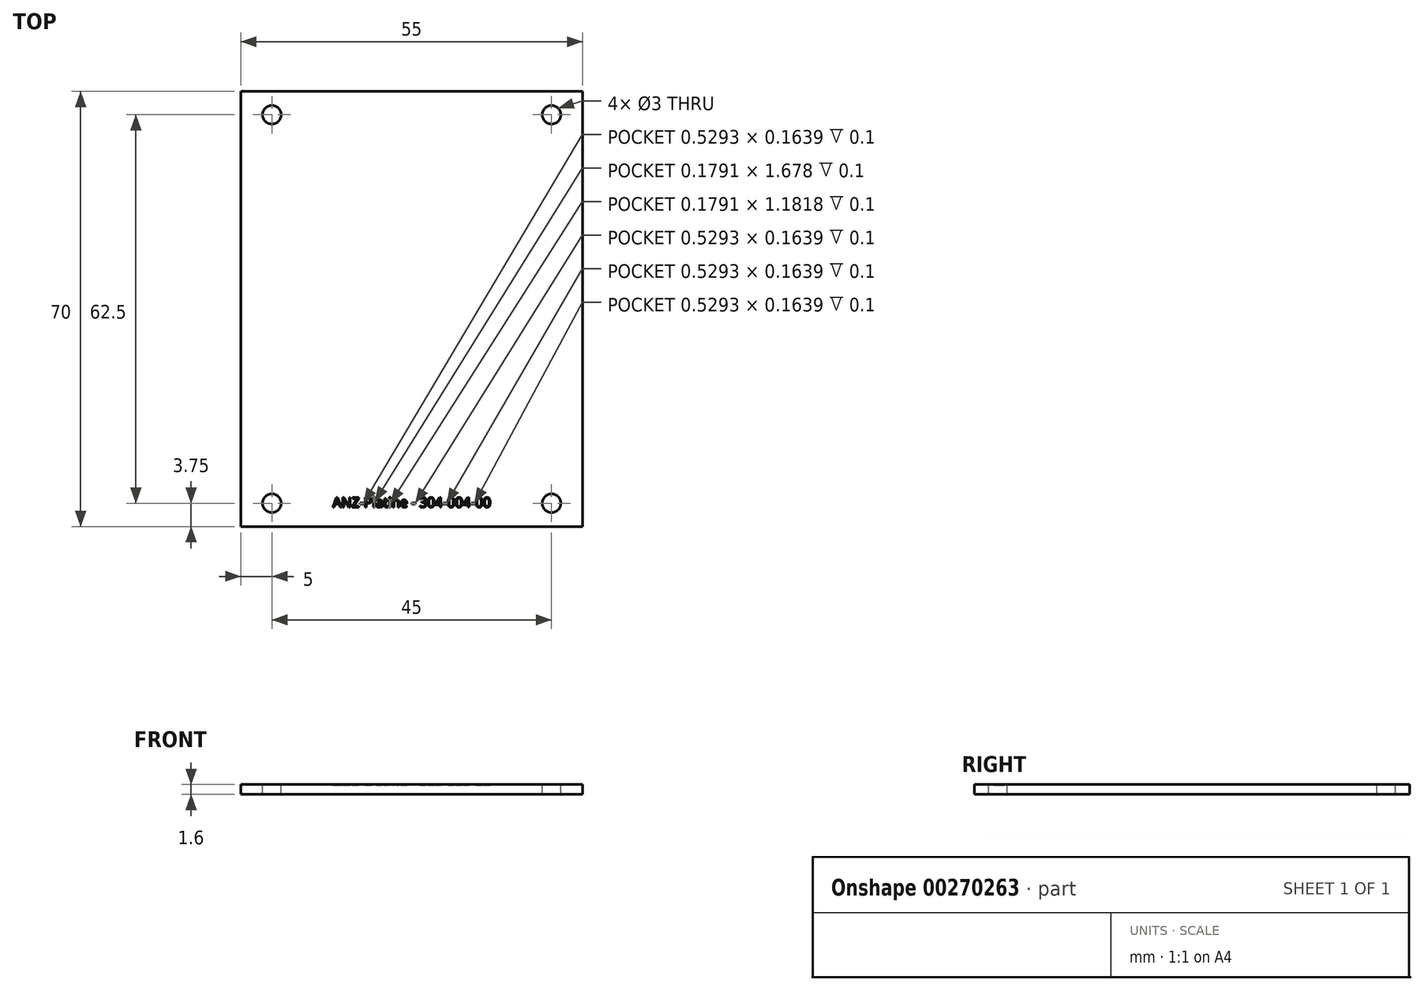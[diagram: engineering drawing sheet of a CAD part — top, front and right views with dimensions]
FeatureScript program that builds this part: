
annotation { "Feature Type Name" : "Feature", "Feature Type Description" : "" }
export const myFeature = defineFeature(function(context is Context, id is Id, definition is map)
    precondition{}
    {
        {
            var Q0;
            Q0=qCreatedBy(makeId("Top.planeOp"),FACE);
            var sketch = newSketch(context, id + "F0", { "sketchPlane" : qUnion([Q0])});
            skLineSegment(sketch, "E0.bottom", {"start": v(27.5, -35) * mm, "end": v(-27.5, -35) * mm});
            skLineSegment(sketch, "E0.top", {"start": v(27.5, 35) * mm, "end": v(-27.5, 35) * mm});
            skLineSegment(sketch, "E0.left", {"start": v(27.5, -35) * mm, "end": v(27.5, 35) * mm});
            skLineSegment(sketch, "E0.right", {"start": v(-27.5, -35) * mm, "end": v(-27.5, 35) * mm});
            skPoint(sketch, "E0.middle", {"position": v(0, 0) * mm});
            skCircle(sketch, "E1", {"center": v(-22.5, 31.25) * mm, "radius": 1.5 * mm});
            skCircle(sketch, "E2", {"center": v(-22.5, -31.25) * mm, "radius": 1.5 * mm});
            skCircle(sketch, "E3", {"center": v(22.5, 31.25) * mm, "radius": 1.5 * mm});
            skCircle(sketch, "E4", {"center": v(22.5, -31.25) * mm, "radius": 1.5 * mm});
            skLineSegment(sketch, "E5", {"start": v(-27.5, 25) * mm, "end": v(22.5, 25) * mm, "construction": true});
            skLineSegment(sketch, "E6", {"start": v(22.5, 25) * mm, "end": v(22.5, -25) * mm, "construction": true});
            skLineSegment(sketch, "E7", {"start": v(22.5, -25) * mm, "end": v(-27.5, -25) * mm, "construction": true});
            skSolve(sketch);
        }
        {
            var Q0;
            Q0=qSketchRegion(id+"F0",true);
            extrude(context, id + "F1", {"entities" : qUnion([Q0]), "oppositeDirection" : true, "depth" : 1.6 * mm});
        }
        {
            var Q0;
            Q0=makeQuery(id+"F0.imprint","IMPRINT",FACE,{"disambiguationData":[TD([[makeQuery(id+"F0.imprint","IMPRINT",EDGE,{"derivedFrom":sQuery(id+"F0.wireOp",EDGE,"E0.bottom")}),-1.0]])]});
            var sketch = newSketch(context, id + "F2", { "sketchPlane" : qUnion([Q0])});
            skText(sketch, "E8", { "text": "ANZ-Platine - 304-004-00", "fontName": "OpenSans-Regular.ttf"});
            const initialGuessF2  = {"E8": [-0.01272, -0.0319, 1, 0, 0.00159]};
            skSetInitialGuess(sketch, initialGuessF2);
            skSolve(sketch);
        }
        {
            var Q0;
            Q0 = qSketchRegion(id + "F2", true);
            extrude(context, id + "F3", {"entities" : qUnion([Q0]), "operationType" : NewBodyOperationType.REMOVE, "oppositeDirection" : true, "depth" : .1 * mm});
        }
    });
